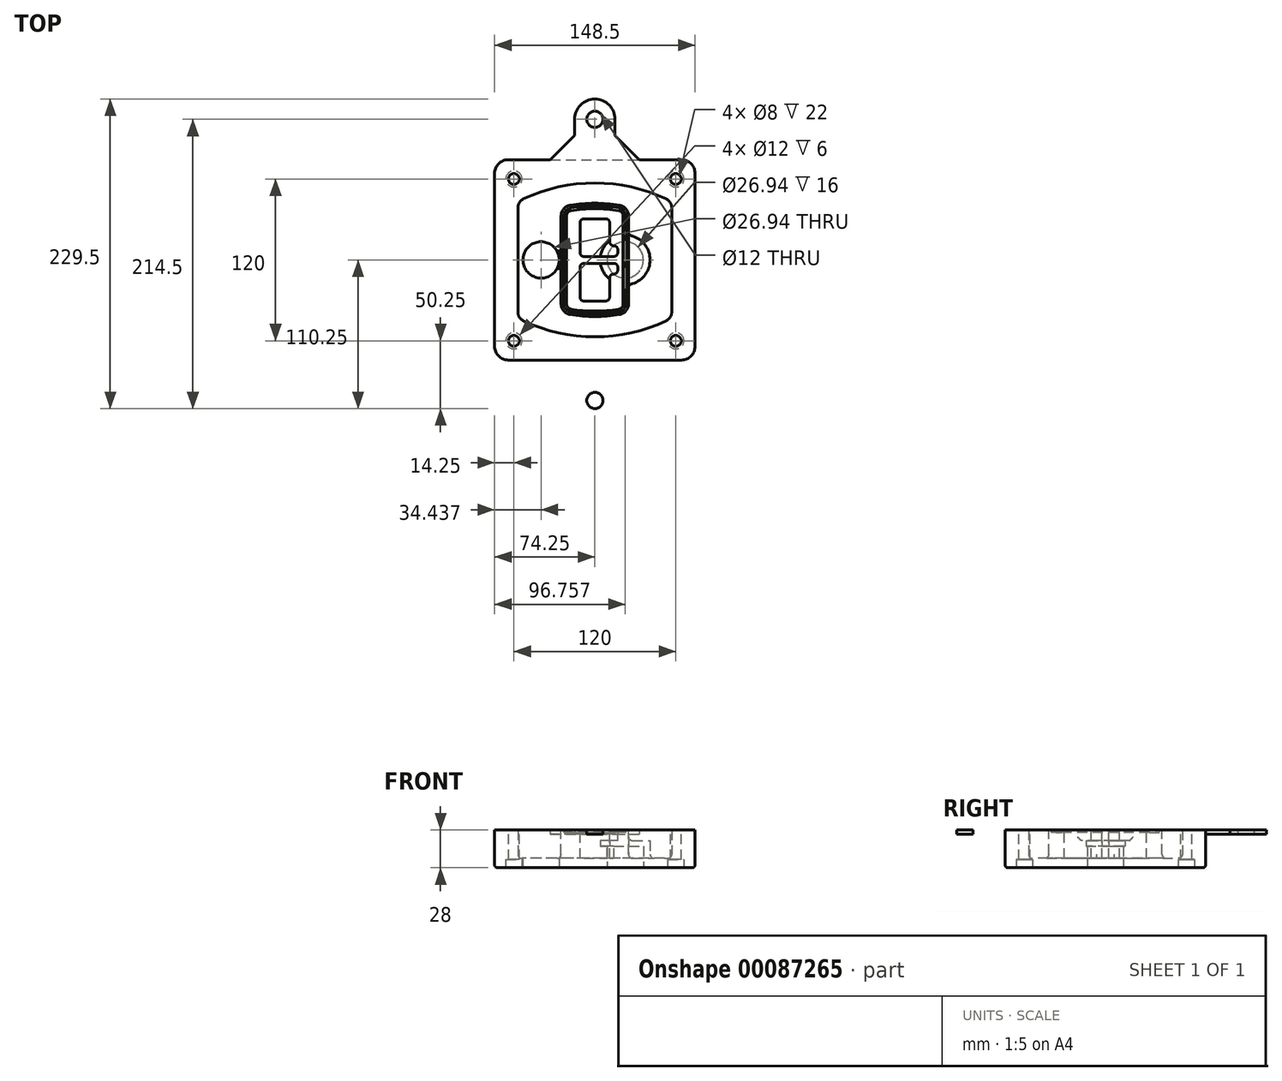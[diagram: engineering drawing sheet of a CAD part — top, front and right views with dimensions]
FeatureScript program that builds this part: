
annotation { "Feature Type Name" : "Feature", "Feature Type Description" : "" }
export const myFeature = defineFeature(function(context is Context, id is Id, definition is map)
    precondition{}
    {
        {
            var Q0;
            Q0=qCreatedBy(makeId("Top.planeOp"),FACE);
            var sketch = newSketch(context, id + "F0", { "sketchPlane" : qUnion([Q0])});
            skPoint(sketch, "E0.rect.middle", {"position": v(0, 0) * mm});
            skLineSegment(sketch, "E1.bottom", {"start": v(-64.25, -74.25) * mm, "end": v(64.25, -74.25) * mm});
            skLineSegment(sketch, "E1.top", {"start": v(-64.25, 74.25) * mm, "end": v(64.25, 74.25) * mm});
            skLineSegment(sketch, "E1.left", {"start": v(-74.25, -64.25) * mm, "end": v(-74.25, 64.25) * mm});
            skLineSegment(sketch, "E1.right", {"start": v(74.25, -64.25) * mm, "end": v(74.25, 64.25) * mm});
            skLineSegment(sketch, "E2", {"start": v(-74.25, 74.25) * mm, "end": v(74.25, -74.25) * mm, "construction": true});
            skLineSegment(sketch, "E3", {"start": v(74.25, 74.25) * mm, "end": v(-74.25, -74.25) * mm, "construction": true});
            skCircle(sketch, "E4", {"center": v(-60, 60) * mm, "radius": 4 * mm});
            skCircle(sketch, "E5", {"center": v(60, 60) * mm, "radius": 4 * mm});
            skCircle(sketch, "E6", {"center": v(60, -60) * mm, "radius": 4 * mm});
            skCircle(sketch, "E7", {"center": v(-60, -60) * mm, "radius": 4 * mm});
            skLineSegment(sketch, "E8", {"start": v(-60, 60) * mm, "end": v(60, 60) * mm, "construction": true});
            skLineSegment(sketch, "E9", {"start": v(60, 60) * mm, "end": v(60, -60) * mm, "construction": true});
            skLineSegment(sketch, "E10", {"start": v(60, -60) * mm, "end": v(-60, -60) * mm, "construction": true});
            skLineSegment(sketch, "E11", {"start": v(-60, -60) * mm, "end": v(-60, 60) * mm, "construction": true});
            skLineSegment(sketch, "E12", {"start": v(-60, 38.83) * mm, "end": v(-60, -38.83) * mm});
            skLineSegment(sketch, "E13", {"start": v(60, 38.83) * mm, "end": v(60, -38.83) * mm});
            skArc(sketch, "E14", {"start": v(54.26, 47.88) * mm, "mid": v(0, 60) * mm, "end": v(-54.26, 47.88) * mm});
            skArc(sketch, "E15", {"start": v(-54.26, -47.88) * mm, "mid": v(0, -60) * mm, "end": v(54.26, -47.88) * mm});
            skLineSegment(sketch, "E16", {"start": v(-60, 0) * mm, "end": v(60, 0) * mm, "construction": true});
            skPoint(sketch, "E17.visualSharp", {"position": v(-60, -45) * mm});
            skArc(sketch, "E17.filletArc", {"start": v(-60, -38.83) * mm, "mid": v(-58.44, -44.2) * mm, "end": v(-54.26, -47.88) * mm});
            skPoint(sketch, "E18.visualSharp", {"position": v(-60, 45) * mm});
            skArc(sketch, "E18.filletArc", {"start": v(-54.26, 47.88) * mm, "mid": v(-58.44, 44.2) * mm, "end": v(-60, 38.83) * mm});
            skPoint(sketch, "E19.visualSharp", {"position": v(60, 45) * mm});
            skArc(sketch, "E19.filletArc", {"start": v(60, 38.83) * mm, "mid": v(58.44, 44.2) * mm, "end": v(54.26, 47.88) * mm});
            skPoint(sketch, "E20.visualSharp", {"position": v(60, -45) * mm});
            skArc(sketch, "E20.filletArc", {"start": v(54.26, -47.88) * mm, "mid": v(58.44, -44.2) * mm, "end": v(60, -38.83) * mm});
            skPoint(sketch, "E21.visualSharp", {"position": v(-74.25, 74.25) * mm});
            skArc(sketch, "E21.filletArc", {"start": v(-64.25, 74.25) * mm, "mid": v(-71.32, 71.32) * mm, "end": v(-74.25, 64.25) * mm});
            skPoint(sketch, "E22.visualSharp", {"position": v(74.25, 74.25) * mm});
            skArc(sketch, "E22.filletArc", {"start": v(74.25, 64.25) * mm, "mid": v(71.32, 71.32) * mm, "end": v(64.25, 74.25) * mm});
            skPoint(sketch, "E23.visualSharp", {"position": v(74.25, -74.25) * mm});
            skArc(sketch, "E23.filletArc", {"start": v(64.25, -74.25) * mm, "mid": v(71.32, -71.32) * mm, "end": v(74.25, -64.25) * mm});
            skPoint(sketch, "E24.visualSharp", {"position": v(-74.25, -74.25) * mm});
            skArc(sketch, "E24.filletArc", {"start": v(-74.25, -64.25) * mm, "mid": v(-71.32, -71.32) * mm, "end": v(-64.25, -74.25) * mm});
            skArc(sketch, "E25.0", {"start": v(57, 38.83) * mm, "mid": v(55.9, 42.58) * mm, "end": v(52.98, 45.17) * mm});
            skLineSegment(sketch, "E25.1", {"start": v(57, 38.83) * mm, "end": v(57, -38.83) * mm});
            skArc(sketch, "E25.2", {"start": v(52.98, -45.17) * mm, "mid": v(55.9, -42.58) * mm, "end": v(57, -38.83) * mm});
            skArc(sketch, "E25.3", {"start": v(-52.98, -45.17) * mm, "mid": v(0, -57) * mm, "end": v(52.98, -45.17) * mm});
            skArc(sketch, "E25.4", {"start": v(-57, -38.83) * mm, "mid": v(-55.9, -42.58) * mm, "end": v(-52.98, -45.17) * mm});
            skArc(sketch, "E25.5", {"start": v(52.98, 45.17) * mm, "mid": v(0, 57) * mm, "end": v(-52.98, 45.17) * mm});
            skLineSegment(sketch, "E25.6", {"start": v(-57, 38.83) * mm, "end": v(-57, -38.83) * mm});
            skArc(sketch, "E25.7", {"start": v(-52.98, 45.17) * mm, "mid": v(-55.9, 42.58) * mm, "end": v(-57, 38.83) * mm});
            skArc(sketch, "E26.0", {"start": v(-55.96, 51.5) * mm, "mid": v(-61.82, 46.33) * mm, "end": v(-64, 38.83) * mm});
            skArc(sketch, "E26.1", {"start": v(55.96, 51.5) * mm, "mid": v(0, 64) * mm, "end": v(-55.96, 51.5) * mm});
            skArc(sketch, "E26.2", {"start": v(64, 38.83) * mm, "mid": v(61.82, 46.33) * mm, "end": v(55.96, 51.5) * mm});
            skLineSegment(sketch, "E26.3", {"start": v(64, 38.83) * mm, "end": v(64, -38.83) * mm});
            skArc(sketch, "E26.4", {"start": v(55.96, -51.5) * mm, "mid": v(61.82, -46.33) * mm, "end": v(64, -38.83) * mm});
            skLineSegment(sketch, "E26.5", {"start": v(-64, 38.83) * mm, "end": v(-64, -38.83) * mm});
            skArc(sketch, "E26.6", {"start": v(-55.96, -51.5) * mm, "mid": v(0, -64) * mm, "end": v(55.96, -51.5) * mm});
            skArc(sketch, "E26.7", {"start": v(-64, -38.83) * mm, "mid": v(-61.82, -46.33) * mm, "end": v(-55.96, -51.5) * mm});
            skSolve(sketch);
        }
        {
            var Q0;
            Q0=makeQuery(id+"F0.imprint","IMPRINT",FACE,{"disambiguationData":[TD([[makeQuery(id+"F0.imprint","IMPRINT",EDGE,{"derivedFrom":sQuery(id+"F0.wireOp",EDGE,"E1.bottom")}),1.0]])]});
            var Q1;
            Q1=makeQuery(id+"F0.imprint","IMPRINT",FACE,{"disambiguationData":[TD([[makeQuery(id+"F0.imprint","IMPRINT",EDGE,{"derivedFrom":sQuery(id+"F0.wireOp",EDGE,"E12")}),1.0]])]});
            var Q2;
            Q2=makeQuery(id+"F0.imprint","IMPRINT",FACE,{"disambiguationData":[TD([[makeQuery(id+"F0.imprint","IMPRINT",EDGE,{"derivedFrom":sQuery(id+"F0.wireOp",EDGE,"E25.0")}),1.0]])]});
            var Q3;
            Q3=makeQuery(id+"F0.imprint","IMPRINT",FACE,{"disambiguationData":[TD([[makeQuery(id+"F0.imprint","IMPRINT",EDGE,{"derivedFrom":sQuery(id+"F0.wireOp",EDGE,"E12")}),-1.0]])]});
            extrude(context, id + "F1", {"entities" : qUnion([Q0, Q1, Q2, Q3]), "oppositeDirection" : true, "depth" : 25 * mm});
        }
        {
            var Q0;
            Q0=makeQuery(id+"F0.imprint","IMPRINT",FACE,{"disambiguationData":[TD([[makeQuery(id+"F0.imprint","IMPRINT",EDGE,{"derivedFrom":sQuery(id+"F0.wireOp",EDGE,"E12")}),1.0]])]});
            extrude(context, id + "F2", {"entities" : qUnion([Q0]), "operationType" : NewBodyOperationType.ADD, "depth" : 3 * mm});
        }
        {
            var Q0;
            Q0=makeQuery(id+"F0.imprint","IMPRINT",FACE,{"disambiguationData":[TD([[makeQuery(id+"F0.imprint","IMPRINT",EDGE,{"derivedFrom":sQuery(id+"F0.wireOp",EDGE,"E25.0")}),1.0]])]});
            extrude(context, id + "F3", {"entities" : qUnion([Q0]), "operationType" : NewBodyOperationType.REMOVE, "oppositeDirection" : true, "depth" : 18 * mm});
        }
        {
            var Q0;
            Q0=makeQuery(id+"F2.opExtrude","CAP_FACE",FACE,{"disambiguationData":[OSD([sQuery(id+"F0.wireOp",EDGE,"E12"),sQuery(id+"F0.wireOp",EDGE,"E13"),sQuery(id+"F0.wireOp",EDGE,"E14"),sQuery(id+"F0.wireOp",EDGE,"E15"),sQuery(id+"F0.wireOp",EDGE,"E17.filletArc"),sQuery(id+"F0.wireOp",EDGE,"E18.filletArc"),sQuery(id+"F0.wireOp",EDGE,"E19.filletArc"),sQuery(id+"F0.wireOp",EDGE,"E20.filletArc"),sQuery(id+"F0.wireOp",EDGE,"E25.0"),sQuery(id+"F0.wireOp",EDGE,"E25.1"),sQuery(id+"F0.wireOp",EDGE,"E25.2"),sQuery(id+"F0.wireOp",EDGE,"E25.3"),sQuery(id+"F0.wireOp",EDGE,"E25.4"),sQuery(id+"F0.wireOp",EDGE,"E25.5"),sQuery(id+"F0.wireOp",EDGE,"E25.6"),sQuery(id+"F0.wireOp",EDGE,"E25.7")])],"isStart":false});
            var sketch = newSketch(context, id + "F4", { "sketchPlane" : qUnion([Q0])});
            skArc(sketch, "E27.0", {"start": v(-18.34, -40.45) * mm, "mid": v(0, -42) * mm, "end": v(18.34, -40.45) * mm});
            skArc(sketch, "E28.0", {"start": v(18.34, 40.45) * mm, "mid": v(0, 42) * mm, "end": v(-18.34, 40.45) * mm});
            skLineSegment(sketch, "E29", {"start": v(-25, 32.57) * mm, "end": v(-25, -32.57) * mm});
            skLineSegment(sketch, "E30", {"start": v(25, 32.57) * mm, "end": v(25, -32.57) * mm});
            skLineSegment(sketch, "E31", {"start": v(-25, 39.1) * mm, "end": v(25, 39.1) * mm, "construction": true});
            skLineSegment(sketch, "E32", {"start": v(-25, -39.1) * mm, "end": v(25, -39.1) * mm, "construction": true});
            skPoint(sketch, "E33.visualSharp", {"position": v(-25, 39.1) * mm});
            skArc(sketch, "E33.filletArc", {"start": v(-18.34, 40.45) * mm, "mid": v(-23.11, 37.73) * mm, "end": v(-25, 32.57) * mm});
            skPoint(sketch, "E34.visualSharp", {"position": v(25, 39.1) * mm});
            skArc(sketch, "E34.filletArc", {"start": v(25, 32.57) * mm, "mid": v(23.11, 37.73) * mm, "end": v(18.34, 40.45) * mm});
            skPoint(sketch, "E35.visualSharp", {"position": v(25, -39.1) * mm});
            skArc(sketch, "E35.filletArc", {"start": v(18.34, -40.45) * mm, "mid": v(23.11, -37.73) * mm, "end": v(25, -32.57) * mm});
            skPoint(sketch, "E36.visualSharp", {"position": v(-25, -39.1) * mm});
            skArc(sketch, "E36.filletArc", {"start": v(-25, -32.57) * mm, "mid": v(-23.11, -37.73) * mm, "end": v(-18.34, -40.45) * mm});
            skArc(sketch, "E37.0", {"start": v(52.98, 45.17) * mm, "mid": v(0, 57) * mm, "end": v(-52.98, 45.17) * mm});
            skArc(sketch, "E37.1", {"start": v(-52.98, 45.17) * mm, "mid": v(-55.9, 42.58) * mm, "end": v(-57, 38.83) * mm});
            skLineSegment(sketch, "E37.2", {"start": v(-57, 38.83) * mm, "end": v(-57, -38.83) * mm});
            skArc(sketch, "E37.3", {"start": v(-57, -38.83) * mm, "mid": v(-55.9, -42.58) * mm, "end": v(-52.98, -45.17) * mm});
            skArc(sketch, "E37.4", {"start": v(-52.98, -45.17) * mm, "mid": v(0, -57) * mm, "end": v(52.98, -45.17) * mm});
            skArc(sketch, "E37.5", {"start": v(52.98, -45.17) * mm, "mid": v(55.9, -42.58) * mm, "end": v(57, -38.83) * mm});
            skLineSegment(sketch, "E37.6", {"start": v(57, 38.83) * mm, "end": v(57, -38.83) * mm});
            skArc(sketch, "E37.7", {"start": v(57, 38.83) * mm, "mid": v(55.9, 42.58) * mm, "end": v(52.98, 45.17) * mm});
            skLineSegment(sketch, "E38.0", {"start": v(23, 32.57) * mm, "end": v(23, -32.57) * mm});
            skArc(sketch, "E38.1", {"start": v(18, -38.48) * mm, "mid": v(21.58, -36.44) * mm, "end": v(23, -32.57) * mm});
            skArc(sketch, "E38.2", {"start": v(-18, -38.48) * mm, "mid": v(0, -40) * mm, "end": v(18, -38.48) * mm});
            skArc(sketch, "E38.3", {"start": v(-23, -32.57) * mm, "mid": v(-21.58, -36.44) * mm, "end": v(-18, -38.48) * mm});
            skLineSegment(sketch, "E38.4", {"start": v(-23, 32.57) * mm, "end": v(-23, -32.57) * mm});
            skArc(sketch, "E38.5", {"start": v(23, 32.57) * mm, "mid": v(21.58, 36.44) * mm, "end": v(18, 38.48) * mm});
            skArc(sketch, "E38.6", {"start": v(-18, 38.48) * mm, "mid": v(-21.58, 36.44) * mm, "end": v(-23, 32.57) * mm});
            skArc(sketch, "E38.7", {"start": v(18, 38.48) * mm, "mid": v(0, 40) * mm, "end": v(-18, 38.48) * mm});
            skArc(sketch, "E39.0", {"start": v(21, 32.57) * mm, "mid": v(20.06, 35.15) * mm, "end": v(17.67, 36.5) * mm});
            skLineSegment(sketch, "E39.1", {"start": v(21, 32.57) * mm, "end": v(21, -32.57) * mm});
            skArc(sketch, "E39.2", {"start": v(17.67, -36.5) * mm, "mid": v(20.06, -35.15) * mm, "end": v(21, -32.57) * mm});
            skArc(sketch, "E39.3", {"start": v(-17.67, -36.5) * mm, "mid": v(0, -38) * mm, "end": v(17.67, -36.5) * mm});
            skArc(sketch, "E39.4", {"start": v(-21, -32.57) * mm, "mid": v(-20.06, -35.15) * mm, "end": v(-17.67, -36.5) * mm});
            skArc(sketch, "E39.5", {"start": v(17.67, 36.5) * mm, "mid": v(0, 38) * mm, "end": v(-17.67, 36.5) * mm});
            skLineSegment(sketch, "E39.6", {"start": v(-21, 32.57) * mm, "end": v(-21, -32.57) * mm});
            skArc(sketch, "E39.7", {"start": v(-17.67, 36.5) * mm, "mid": v(-20.06, 35.15) * mm, "end": v(-21, 32.57) * mm});
            skLineSegment(sketch, "E40", {"start": v(-25, 0) * mm, "end": v(25, 0) * mm, "construction": true});
            skLineSegment(sketch, "E41", {"start": v(-11, 5.5) * mm, "end": v(-11, 27.5) * mm});
            skLineSegment(sketch, "E42", {"start": v(-8, 30.5) * mm, "end": v(8, 30.5) * mm});
            skLineSegment(sketch, "E43", {"start": v(11, 27.5) * mm, "end": v(11, 13.5) * mm});
            skLineSegment(sketch, "E44", {"start": v(14, 10.5) * mm, "end": v(14, 10.5) * mm});
            skLineSegment(sketch, "E45", {"start": v(17, 7.5) * mm, "end": v(17, 5.5) * mm});
            skLineSegment(sketch, "E46", {"start": v(14, 2.5) * mm, "end": v(-8, 2.5) * mm});
            skPoint(sketch, "E47.visualSharp", {"position": v(-11, 30.5) * mm});
            skArc(sketch, "E47.filletArc", {"start": v(-8, 30.5) * mm, "mid": v(-10.12, 29.62) * mm, "end": v(-11, 27.5) * mm});
            skPoint(sketch, "E48.visualSharp", {"position": v(11, 30.5) * mm});
            skArc(sketch, "E48.filletArc", {"start": v(11, 27.5) * mm, "mid": v(10.12, 29.62) * mm, "end": v(8, 30.5) * mm});
            skPoint(sketch, "E49.visualSharp", {"position": v(11, 10.5) * mm});
            skArc(sketch, "E49.filletArc", {"start": v(11, 13.5) * mm, "mid": v(11.88, 11.38) * mm, "end": v(14, 10.5) * mm});
            skPoint(sketch, "E50.visualSharp", {"position": v(17, 10.5) * mm});
            skArc(sketch, "E50.filletArc", {"start": v(17, 7.5) * mm, "mid": v(16.12, 9.62) * mm, "end": v(14, 10.5) * mm});
            skPoint(sketch, "E51.visualSharp", {"position": v(17, 2.5) * mm});
            skArc(sketch, "E51.filletArc", {"start": v(14, 2.5) * mm, "mid": v(16.12, 3.38) * mm, "end": v(17, 5.5) * mm});
            skPoint(sketch, "E52.visualSharp", {"position": v(-11, 2.5) * mm});
            skArc(sketch, "E52.filletArc", {"start": v(-11, 5.5) * mm, "mid": v(-10.12, 3.38) * mm, "end": v(-8, 2.5) * mm});
            skLineSegment(sketch, "E53.0.MirrorCS", {"start": v(14, -2.5) * mm, "end": v(-8, -2.5) * mm});
            skArc(sketch, "E54.0.MirrorCS", {"start": v(-11, -5.5) * mm, "mid": v(-10.12, -3.38) * mm, "end": v(-8, -2.5) * mm});
            skLineSegment(sketch, "E55.0.MirrorCS", {"start": v(-11, -5.5) * mm, "end": v(-11, -27.5) * mm});
            skArc(sketch, "E56.0.MirrorCS", {"start": v(-8, -30.5) * mm, "mid": v(-10.12, -29.62) * mm, "end": v(-11, -27.5) * mm});
            skLineSegment(sketch, "E57.0.MirrorCS", {"start": v(-8, -30.5) * mm, "end": v(8, -30.5) * mm});
            skArc(sketch, "E58.0.MirrorCS", {"start": v(11, -27.5) * mm, "mid": v(10.12, -29.62) * mm, "end": v(8, -30.5) * mm});
            skLineSegment(sketch, "E59.0.MirrorCS", {"start": v(11, -27.5) * mm, "end": v(11, -13.5) * mm});
            skArc(sketch, "E60.0.MirrorCS", {"start": v(11, -13.5) * mm, "mid": v(11.88, -11.38) * mm, "end": v(14, -10.5) * mm});
            skArc(sketch, "E61.0.MirrorCS", {"start": v(17, -7.5) * mm, "mid": v(16.12, -9.62) * mm, "end": v(14, -10.5) * mm});
            skLineSegment(sketch, "E62.0.MirrorCS", {"start": v(17, -7.5) * mm, "end": v(17, -5.5) * mm});
            skArc(sketch, "E63.0.MirrorCS", {"start": v(14, -2.5) * mm, "mid": v(16.12, -3.38) * mm, "end": v(17, -5.5) * mm});
            skSolve(sketch);
        }
        {
            var Q0;
            Q0=makeQuery(id+"F4.imprint","IMPRINT",FACE,{"disambiguationData":[TD([[makeQuery(id+"F4.imprint","IMPRINT",EDGE,{"derivedFrom":sQuery(id+"F4.wireOp",EDGE,"E27.0")}),1.0]])]});
            var Q1;
            Q1=makeQuery(id+"F4.imprint","IMPRINT",FACE,{"disambiguationData":[TD([[makeQuery(id+"F4.imprint","IMPRINT",EDGE,{"derivedFrom":sQuery(id+"F4.wireOp",EDGE,"E38.0")}),-1.0]])]});
            var Q2;
            Q2=makeQuery(id+"F4.imprint","IMPRINT",FACE,{"disambiguationData":[TD([[makeQuery(id+"F4.imprint","IMPRINT",EDGE,{"derivedFrom":sQuery(id+"F4.wireOp",EDGE,"E39.0")}),1.0]])]});
            extrude(context, id + "F5", {"entities" : qUnion([Q0, Q1, Q2]), "operationType" : NewBodyOperationType.ADD, "endBound" : BoundingType.UP_TO_NEXT, "oppositeDirection" : true, "depth" : 25 * mm});
        }
        {
            var Q0;
            Q0=makeQuery(id+"F4.imprint","IMPRINT",FACE,{"disambiguationData":[TD([[makeQuery(id+"F4.imprint","IMPRINT",EDGE,{"derivedFrom":sQuery(id+"F4.wireOp",EDGE,"E38.0")}),-1.0]])]});
            extrude(context, id + "F6", {"entities" : qUnion([Q0]), "operationType" : NewBodyOperationType.REMOVE, "oppositeDirection" : true, "depth" : 2 * mm});
        }
        {
            var Q0;
            Q0=makeQuery(id+"F1.opExtrude","CAP_FACE",FACE,{"disambiguationData":[OSD([sQuery(id+"F0.wireOp",EDGE,"E1.bottom"),sQuery(id+"F0.wireOp",EDGE,"E1.top"),sQuery(id+"F0.wireOp",EDGE,"E1.left"),sQuery(id+"F0.wireOp",EDGE,"E1.right"),sQuery(id+"F0.wireOp",EDGE,"E4"),sQuery(id+"F0.wireOp",EDGE,"E5"),sQuery(id+"F0.wireOp",EDGE,"E6"),sQuery(id+"F0.wireOp",EDGE,"E7"),sQuery(id+"F0.wireOp",EDGE,"E21.filletArc"),sQuery(id+"F0.wireOp",EDGE,"E22.filletArc"),sQuery(id+"F0.wireOp",EDGE,"E23.filletArc"),sQuery(id+"F0.wireOp",EDGE,"E24.filletArc")])],"isStart":false});
            var sketch = newSketch(context, id + "F7", { "sketchPlane" : qUnion([Q0])});
            skCircle(sketch, "E64", {"center": v(22.5, 0) * mm, "radius": 13.47 * mm});
            skCircle(sketch, "E65", {"center": v(-39.81, 0) * mm, "radius": 13.47 * mm});
            skLineSegment(sketch, "E66", {"start": v(74.25, 0) * mm, "end": v(-74.25, 0) * mm});
            skCircle(sketch, "E67", {"center": v(22.5, 0) * mm, "radius": 18.47 * mm});
            skCircle(sketch, "E68", {"center": v(60, -60) * mm, "radius": 6 * mm});
            skCircle(sketch, "E69", {"center": v(-60, -60) * mm, "radius": 6 * mm});
            skCircle(sketch, "E70", {"center": v(-60, 60) * mm, "radius": 6 * mm});
            skCircle(sketch, "E71", {"center": v(60, 60) * mm, "radius": 6 * mm});
            skSolve(sketch);
        }
        {
            var Q0;
            {var subQ1=sQuery(id+"F7.wireOp",EDGE,"E66");var subQ4=sQuery(id+"F7.wireOp",EDGE,"E64");var subQ6=makeQuery(id+"F7.imprint","INTERSECT",VERTEX,{"disambiguationData":[OD(0.0)],"derivedFrom":[subQ4,subQ1]});Q0=makeQuery(id+"F7.imprint","IMPRINT",FACE,{"disambiguationData":[TD([[makeQuery(id+"F7.imprint","IMPRINT",EDGE,{"disambiguationData":[TD([[subQ6,-1.0]])],"derivedFrom":subQ4}),-1.0]])]});}
            var Q1;
            {var subQ0=sQuery(id+"F7.wireOp",EDGE,"E66");var subQ1=sQuery(id+"F7.wireOp",EDGE,"E64");var subQ3=makeQuery(id+"F7.imprint","INTERSECT",VERTEX,{"disambiguationData":[OD(0.0)],"derivedFrom":[subQ1,subQ0]});Q1=makeQuery(id+"F7.imprint","IMPRINT",FACE,{"disambiguationData":[TD([[makeQuery(id+"F7.imprint","IMPRINT",EDGE,{"disambiguationData":[TD([[subQ3,-1.0]])],"derivedFrom":subQ1}),1.0]])]});}
            var Q2;
            {var subQ0=sQuery(id+"F7.wireOp",EDGE,"E66");var subQ1=sQuery(id+"F7.wireOp",EDGE,"E64");var subQ3=makeQuery(id+"F7.imprint","INTERSECT",VERTEX,{"disambiguationData":[OD(0.0)],"derivedFrom":[subQ1,subQ0]});Q2=makeQuery(id+"F7.imprint","IMPRINT",FACE,{"disambiguationData":[TD([[makeQuery(id+"F7.imprint","IMPRINT",EDGE,{"disambiguationData":[TD([[subQ3,1.0]])],"derivedFrom":subQ1}),1.0]])]});}
            var Q3;
            {var subQ1=sQuery(id+"F7.wireOp",EDGE,"E66");var subQ4=sQuery(id+"F7.wireOp",EDGE,"E64");var subQ6=makeQuery(id+"F7.imprint","INTERSECT",VERTEX,{"disambiguationData":[OD(0.0)],"derivedFrom":[subQ4,subQ1]});Q3=makeQuery(id+"F7.imprint","IMPRINT",FACE,{"disambiguationData":[TD([[makeQuery(id+"F7.imprint","IMPRINT",EDGE,{"disambiguationData":[TD([[subQ6,1.0]])],"derivedFrom":subQ4}),-1.0]])]});}
            extrude(context, id + "F8", {"entities" : qUnion([Q0, Q1, Q2, Q3]), "operationType" : NewBodyOperationType.ADD, "oppositeDirection" : true, "depth" : 20 * mm});
        }
        {
            var Q0;
            {var subQ0=sQuery(id+"F7.wireOp",EDGE,"E66");var subQ1=sQuery(id+"F7.wireOp",EDGE,"E64");var subQ3=makeQuery(id+"F7.imprint","INTERSECT",VERTEX,{"disambiguationData":[OD(0.0)],"derivedFrom":[subQ1,subQ0]});Q0=makeQuery(id+"F7.imprint","IMPRINT",FACE,{"disambiguationData":[TD([[makeQuery(id+"F7.imprint","IMPRINT",EDGE,{"disambiguationData":[TD([[subQ3,-1.0]])],"derivedFrom":subQ1}),1.0]])]});}
            var Q1;
            {var subQ0=sQuery(id+"F7.wireOp",EDGE,"E66");var subQ1=sQuery(id+"F7.wireOp",EDGE,"E64");var subQ3=makeQuery(id+"F7.imprint","INTERSECT",VERTEX,{"disambiguationData":[OD(0.0)],"derivedFrom":[subQ1,subQ0]});Q1=makeQuery(id+"F7.imprint","IMPRINT",FACE,{"disambiguationData":[TD([[makeQuery(id+"F7.imprint","IMPRINT",EDGE,{"disambiguationData":[TD([[subQ3,1.0]])],"derivedFrom":subQ1}),1.0]])]});}
            extrude(context, id + "F9", {"entities" : qUnion([Q0, Q1]), "operationType" : NewBodyOperationType.REMOVE, "oppositeDirection" : true, "depth" : 16 * mm});
        }
        {
            var Q0;
            {var subQ0=sQuery(id+"F7.wireOp",EDGE,"E66");var subQ1=sQuery(id+"F7.wireOp",EDGE,"E65");var subQ3=makeQuery(id+"F7.imprint","INTERSECT",VERTEX,{"disambiguationData":[OD(0.0)],"derivedFrom":[subQ1,subQ0]});Q0=makeQuery(id+"F7.imprint","IMPRINT",FACE,{"disambiguationData":[TD([[makeQuery(id+"F7.imprint","IMPRINT",EDGE,{"disambiguationData":[TD([[subQ3,-1.0]])],"derivedFrom":subQ1}),1.0]])]});}
            var Q1;
            {var subQ0=sQuery(id+"F7.wireOp",EDGE,"E66");var subQ1=sQuery(id+"F7.wireOp",EDGE,"E65");var subQ3=makeQuery(id+"F7.imprint","INTERSECT",VERTEX,{"disambiguationData":[OD(0.0)],"derivedFrom":[subQ1,subQ0]});Q1=makeQuery(id+"F7.imprint","IMPRINT",FACE,{"disambiguationData":[TD([[makeQuery(id+"F7.imprint","IMPRINT",EDGE,{"disambiguationData":[TD([[subQ3,1.0]])],"derivedFrom":subQ1}),1.0]])]});}
            extrude(context, id + "F10", {"entities" : qUnion([Q0, Q1]), "operationType" : NewBodyOperationType.REMOVE, "oppositeDirection" : true, "depth" : 25 * mm});
        }
        {
            var Q0;
            Q0=makeQuery(id+"F7.imprint","IMPRINT",FACE,{"disambiguationData":[TD([[makeQuery(id+"F7.imprint","IMPRINT",EDGE,{"derivedFrom":sQuery(id+"F7.wireOp",EDGE,"E68")}),1.0]])]});
            var Q1;
            Q1=makeQuery(id+"F7.imprint","IMPRINT",FACE,{"disambiguationData":[TD([[makeQuery(id+"F7.imprint","IMPRINT",EDGE,{"derivedFrom":makeQuery(id+"F1.opExtrude","CAP_EDGE",EDGE,{"disambiguationData":[OSD([sQuery(id+"F0.wireOp",EDGE,"E5")])],"isStart":false})}),-1.0]])]});
            var Q2;
            Q2=makeQuery(id+"F7.imprint","IMPRINT",FACE,{"disambiguationData":[TD([[makeQuery(id+"F7.imprint","IMPRINT",EDGE,{"derivedFrom":sQuery(id+"F7.wireOp",EDGE,"E69")}),1.0]])]});
            var Q3;
            Q3=makeQuery(id+"F7.imprint","IMPRINT",FACE,{"disambiguationData":[TD([[makeQuery(id+"F7.imprint","IMPRINT",EDGE,{"derivedFrom":makeQuery(id+"F1.opExtrude","CAP_EDGE",EDGE,{"disambiguationData":[OSD([sQuery(id+"F0.wireOp",EDGE,"E4")])],"isStart":false})}),-1.0]])]});
            var Q4;
            Q4=makeQuery(id+"F7.imprint","IMPRINT",FACE,{"disambiguationData":[TD([[makeQuery(id+"F7.imprint","IMPRINT",EDGE,{"derivedFrom":sQuery(id+"F7.wireOp",EDGE,"E70")}),1.0]])]});
            var Q5;
            Q5=makeQuery(id+"F7.imprint","IMPRINT",FACE,{"disambiguationData":[TD([[makeQuery(id+"F7.imprint","IMPRINT",EDGE,{"derivedFrom":makeQuery(id+"F1.opExtrude","CAP_EDGE",EDGE,{"disambiguationData":[OSD([sQuery(id+"F0.wireOp",EDGE,"E7")])],"isStart":false})}),-1.0]])]});
            var Q6;
            Q6=makeQuery(id+"F7.imprint","IMPRINT",FACE,{"disambiguationData":[TD([[makeQuery(id+"F7.imprint","IMPRINT",EDGE,{"derivedFrom":sQuery(id+"F7.wireOp",EDGE,"E71")}),1.0]])]});
            var Q7;
            Q7=makeQuery(id+"F7.imprint","IMPRINT",FACE,{"disambiguationData":[TD([[makeQuery(id+"F7.imprint","IMPRINT",EDGE,{"derivedFrom":makeQuery(id+"F1.opExtrude","CAP_EDGE",EDGE,{"disambiguationData":[OSD([sQuery(id+"F0.wireOp",EDGE,"E6")])],"isStart":false})}),-1.0]])]});
            extrude(context, id + "F11", {"entities" : qUnion([Q0, Q1, Q2, Q3, Q4, Q5, Q6, Q7]), "operationType" : NewBodyOperationType.REMOVE, "oppositeDirection" : true, "depth" : 6 * mm});
        }
        {
            var Q0;
            Q0=makeQuery(id+"F9.boolean.opBoolean","COPY",FACE,{"derivedFrom":makeQuery(id+"F9.opExtrude","CAP_FACE",FACE,{"disambiguationData":[OSD([sQuery(id+"F7.wireOp",EDGE,"E64")])],"isStart":false})});
            var sketch = newSketch(context, id + "F12", { "sketchPlane" : qUnion([Q0])});
            skArc(sketch, "E72.0", {"start": v(11, 14.45) * mm, "mid": v(6.45, 9.13) * mm, "end": v(4.2, 2.5) * mm});
            skArc(sketch, "E72.1", {"start": v(4.2, -2.5) * mm, "mid": v(6.45, -9.13) * mm, "end": v(11, -14.45) * mm});
            skLineSegment(sketch, "E73", {"start": v(4.2, -2.5) * mm, "end": v(14, -2.5) * mm});
            skLineSegment(sketch, "E74.0", {"start": v(14, 2.5) * mm, "end": v(4.2, 2.5) * mm});
            skArc(sketch, "E74.1", {"start": v(14, 2.5) * mm, "mid": v(16.12, 3.38) * mm, "end": v(17, 5.5) * mm});
            skLineSegment(sketch, "E74.2", {"start": v(17, 7.5) * mm, "end": v(17, 5.5) * mm});
            skArc(sketch, "E74.3", {"start": v(17, 7.5) * mm, "mid": v(16.12, 9.62) * mm, "end": v(14, 10.5) * mm});
            skArc(sketch, "E74.4", {"start": v(11, 13.5) * mm, "mid": v(11.88, 11.38) * mm, "end": v(14, 10.5) * mm});
            skLineSegment(sketch, "E74.5", {"start": v(11, 14.45) * mm, "end": v(11, 13.5) * mm});
            skLineSegment(sketch, "E74.7", {"start": v(14, -2.5) * mm, "end": v(4.2, -2.5) * mm});
            skArc(sketch, "E74.8", {"start": v(14, -2.5) * mm, "mid": v(16.12, -3.38) * mm, "end": v(17, -5.5) * mm});
            skLineSegment(sketch, "E74.9", {"start": v(17, -7.5) * mm, "end": v(17, -5.5) * mm});
            skArc(sketch, "E74.10", {"start": v(17, -7.5) * mm, "mid": v(16.12, -9.62) * mm, "end": v(14, -10.5) * mm});
            skArc(sketch, "E74.11", {"start": v(11, -13.5) * mm, "mid": v(11.88, -11.38) * mm, "end": v(14, -10.5) * mm});
            skLineSegment(sketch, "E74.12", {"start": v(11, -14.45) * mm, "end": v(11, -13.5) * mm});
            skPoint(sketch, "E75.orphan", {"position": v(11, -27.5) * mm});
            skPoint(sketch, "E76.orphan", {"position": v(-8, -2.5) * mm});
            skPoint(sketch, "E77.orphan", {"position": v(-8, 2.5) * mm});
            skPoint(sketch, "E78.orphan", {"position": v(11, 27.5) * mm});
            skSolve(sketch);
        }
        {
            var Q0;
            {var subQ7=sQuery(id+"F12.wireOp",EDGE,"E72.0");var subQ14=sQuery(id+"F12.wireOp",EDGE,"E72.1");var subQ16=sQuery(id+"F12.wireOp",EDGE,"E74.1");var subQ18=sQuery(id+"F12.wireOp",EDGE,"E74.8");Q0=qUnion([makeQuery(id+"F12.imprint","IMPRINT",FACE,{"disambiguationData":[TD([[makeQuery(id+"F12.imprint","IMPRINT",EDGE,{"derivedFrom":subQ7}),1.0]])]}),makeQuery(id+"F12.imprint","IMPRINT",FACE,{"disambiguationData":[TD([[makeQuery(id+"F12.imprint","IMPRINT",EDGE,{"derivedFrom":subQ14}),1.0]])]}),makeQuery(id+"F12.imprint","IMPRINT",FACE,{"disambiguationData":[TD([[makeQuery(id+"F12.imprint","IMPRINT",EDGE,{"derivedFrom":subQ16}),1.0]])]}),makeQuery(id+"F12.imprint","IMPRINT",FACE,{"disambiguationData":[TD([[makeQuery(id+"F12.imprint","IMPRINT",EDGE,{"derivedFrom":subQ18}),-1.0]])]})]);}
            var Q1;
            Q1=makeQuery(id+"F5.boolean.opBoolean","SPLIT",FACE,{"disambiguationData":[TD([makeQuery(id+"F5.opExtrude","SWEPT_FACE",FACE,{"disambiguationData":[OSD([sQuery(id+"F4.wireOp",EDGE,"E41")])]})])],"derivedFrom":makeQuery(id+"F3.boolean.opBoolean","COPY",FACE,{"derivedFrom":makeQuery(id+"F3.opExtrude","CAP_FACE",FACE,{"disambiguationData":[OSD([sQuery(id+"F0.wireOp",EDGE,"E25.0"),sQuery(id+"F0.wireOp",EDGE,"E25.1"),sQuery(id+"F0.wireOp",EDGE,"E25.2"),sQuery(id+"F0.wireOp",EDGE,"E25.3"),sQuery(id+"F0.wireOp",EDGE,"E25.4"),sQuery(id+"F0.wireOp",EDGE,"E25.5"),sQuery(id+"F0.wireOp",EDGE,"E25.6"),sQuery(id+"F0.wireOp",EDGE,"E25.7")])],"isStart":false})})});
            extrude(context, id + "F13", {"entities" : qUnion([Q0]), "operationType" : NewBodyOperationType.REMOVE, "endBound" : BoundingType.UP_TO_SURFACE, "endBoundEntityFace" : qUnion([Q1]), "depth" : 25 * mm});
        }
        {
            var Q0;
            Q0=makeQuery(id+"F3.boolean.opBoolean","COPY",EDGE,{"derivedFrom":makeQuery(id+"F3.opExtrude","CAP_EDGE",EDGE,{"disambiguationData":[OSD([sQuery(id+"F0.wireOp",EDGE,"E25.6")])],"isStart":false})});
            var Q1;
            Q1=makeQuery(id+"F8.boolean.opBoolean","INTERSECT",EDGE,{"derivedFrom":[makeQuery(id+"F5.opExtrude","SWEPT_FACE",FACE,{"disambiguationData":[OSD([sQuery(id+"F4.wireOp",EDGE,"E30")])]}),makeQuery(id+"F8.opExtrude","CAP_FACE",FACE,{"disambiguationData":[OSD([sQuery(id+"F7.wireOp",EDGE,"E67")])],"isStart":false})]});
            var Q2;
            Q2=makeQuery(id+"F8.boolean.opBoolean","INTERSECT",EDGE,{"disambiguationData":[OD(1.0)],"derivedFrom":[makeQuery(id+"F5.opExtrude","SWEPT_FACE",FACE,{"disambiguationData":[OSD([sQuery(id+"F4.wireOp",EDGE,"E30")])]}),makeQuery(id+"F8.opExtrude","SWEPT_FACE",FACE,{"disambiguationData":[OSD([sQuery(id+"F7.wireOp",EDGE,"E67")])]})]});
            var Q3;
            {var subQ0=sQuery(id+"F4.wireOp",EDGE,"E30");Q3=makeQuery(id+"F8.boolean.opBoolean","SPLIT",EDGE,{"disambiguationData":[TD([makeQuery(id+"F5.opExtrude","SWEPT_FACE",FACE,{"disambiguationData":[OSD([sQuery(id+"F4.wireOp",EDGE,"E35.filletArc")])]})])],"derivedFrom":makeQuery(id+"F5.opExtrude","CAP_EDGE",EDGE,{"disambiguationData":[OSD([subQ0])],"isStart":false})});}
            var Q4;
            {var subQ0=sQuery(id+"F0.wireOp",EDGE,"E25.7");var subQ1=sQuery(id+"F0.wireOp",EDGE,"E25.1");var subQ2=sQuery(id+"F0.wireOp",EDGE,"E25.6");var subQ3=sQuery(id+"F0.wireOp",EDGE,"E25.5");var subQ4=sQuery(id+"F0.wireOp",EDGE,"E25.4");var subQ5=sQuery(id+"F0.wireOp",EDGE,"E25.0");var subQ6=sQuery(id+"F0.wireOp",EDGE,"E25.2");var subQ7=sQuery(id+"F0.wireOp",EDGE,"E25.3");Q4=makeQuery(id+"F8.boolean.opBoolean","INTERSECT",EDGE,{"derivedFrom":[makeQuery(id+"F5.boolean.opBoolean","SPLIT",FACE,{"disambiguationData":[TD([makeQuery(id+"F2.opExtrude","SWEPT_FACE",FACE,{"disambiguationData":[OSD([subQ5])]})])],"derivedFrom":makeQuery(id+"F3.boolean.opBoolean","COPY",FACE,{"derivedFrom":makeQuery(id+"F3.opExtrude","CAP_FACE",FACE,{"disambiguationData":[OSD([subQ5,subQ1,subQ6,subQ7,subQ4,subQ3,subQ2,subQ0])],"isStart":false})})}),makeQuery(id+"F8.opExtrude","SWEPT_FACE",FACE,{"disambiguationData":[OSD([sQuery(id+"F7.wireOp",EDGE,"E67")])]})]});}
            var Q5;
            Q5=makeQuery(id+"F8.boolean.opBoolean","INTERSECT",EDGE,{"disambiguationData":[OD(0.0)],"derivedFrom":[makeQuery(id+"F5.opExtrude","SWEPT_FACE",FACE,{"disambiguationData":[OSD([sQuery(id+"F4.wireOp",EDGE,"E30")])]}),makeQuery(id+"F8.opExtrude","SWEPT_FACE",FACE,{"disambiguationData":[OSD([sQuery(id+"F7.wireOp",EDGE,"E67")])]})]});
            fillet(context, id + "F14", {"entities" : qUnion([Q0, Q1, Q2, Q3, Q4, Q5]), "radius" : 3 * mm, "tangentPropagation" : true, "allowEdgeOverflow" : false});
        }
        {
            var Q0;
            Q0=makeQuery(id+"F1.opExtrude","CAP_EDGE",EDGE,{"disambiguationData":[OSD([sQuery(id+"F0.wireOp",EDGE,"E1.bottom")])],"isStart":false});
            fillet(context, id + "F15", {"entities" : qUnion([Q0]), "radius" : 2 * mm, "tangentPropagation" : true, "allowEdgeOverflow" : false});
        }
        {
            var Q0;
            {var subQ0=sQuery(id+"F0.wireOp",EDGE,"E22.filletArc");var subQ1=sQuery(id+"F0.wireOp",EDGE,"E7");var subQ2=sQuery(id+"F0.wireOp",EDGE,"E6");var subQ3=sQuery(id+"F0.wireOp",EDGE,"E5");var subQ4=sQuery(id+"F0.wireOp",EDGE,"E4");var subQ5=sQuery(id+"F0.wireOp",EDGE,"E1.bottom");var subQ6=sQuery(id+"F0.wireOp",EDGE,"E21.filletArc");var subQ7=sQuery(id+"F0.wireOp",EDGE,"E1.top");var subQ8=sQuery(id+"F0.wireOp",EDGE,"E1.left");var subQ9=sQuery(id+"F0.wireOp",EDGE,"E1.right");var subQ10=sQuery(id+"F0.wireOp",EDGE,"E23.filletArc");var subQ11=sQuery(id+"F0.wireOp",EDGE,"E24.filletArc");Q0=makeQuery(id+"F2.boolean.opBoolean","SPLIT",FACE,{"disambiguationData":[TD([makeQuery(id+"F1.opExtrude","SWEPT_FACE",FACE,{"disambiguationData":[OSD([subQ5])]})])],"derivedFrom":makeQuery(id+"F1.opExtrude","CAP_FACE",FACE,{"disambiguationData":[OSD([subQ5,subQ7,subQ8,subQ9,subQ4,subQ3,subQ2,subQ1,subQ6,subQ0,subQ10,subQ11])],"isStart":true})});}
            var sketch = newSketch(context, id + "F16", { "sketchPlane" : qUnion([Q0])});
            skCircle(sketch, "E79", {"center": v(0, 104.25) * mm, "radius": 6 * mm});
            skArc(sketch, "E80", {"start": v(15, 104.25) * mm, "mid": v(0, 119.25) * mm, "end": v(-15, 104.25) * mm});
            skLineSegment(sketch, "E81", {"start": v(15, 104.25) * mm, "end": v(15, 92.25) * mm});
            skLineSegment(sketch, "E82", {"start": v(-15, 104.25) * mm, "end": v(-15, 92.25) * mm});
            skLineSegment(sketch, "E83", {"start": v(15, 92.25) * mm, "end": v(33, 74.25) * mm});
            skLineSegment(sketch, "E84", {"start": v(-15, 92.25) * mm, "end": v(-33, 74.25) * mm});
            skCircle(sketch, "E85.MirrorC", {"center": v(0, -104.25) * mm, "radius": 6 * mm});
            skLineSegment(sketch, "E86.MirrorCS", {"start": v(-15, -104.25) * mm, "end": v(-15, -92.25) * mm});
            skLineSegment(sketch, "E87.MirrorCS", {"start": v(15, -92.25) * mm, "end": v(33, -74.25) * mm});
            skLineSegment(sketch, "E88.MirrorCS", {"start": v(-15, -92.25) * mm, "end": v(-33, -74.25) * mm});
            skLineSegment(sketch, "E89.MirrorCS", {"start": v(15, -104.25) * mm, "end": v(15, -92.25) * mm});
            skArc(sketch, "E90.MirrorCS", {"start": v(15, -104.25) * mm, "mid": v(0, -119.25) * mm, "end": v(-15, -104.25) * mm});
            skSolve(sketch);
        }
        {
            var Q0;
            Q0=makeQuery(id+"F16.imprint","IMPRINT",FACE,{"disambiguationData":[TD([[makeQuery(id+"F16.imprint","IMPRINT",EDGE,{"derivedFrom":makeQuery(id+"F1.opExtrude","CAP_EDGE",EDGE,{"disambiguationData":[OSD([sQuery(id+"F0.wireOp",EDGE,"E1.left")])],"isStart":true})}),-1.0]])]});
            var Q1;
            Q1=makeQuery(id+"F16.imprint","IMPRINT",FACE,{"disambiguationData":[TD([[makeQuery(id+"F16.imprint","IMPRINT",EDGE,{"derivedFrom":sQuery(id+"F16.wireOp",EDGE,"E79")}),-1.0]])]});
            var Q2;
            Q2=makeQuery(id+"F16.imprint","IMPRINT",FACE,{"disambiguationData":[TD([[makeQuery(id+"F16.imprint","IMPRINT",EDGE,{"derivedFrom":sQuery(id+"F16.wireOp",EDGE,"E85.MirrorC")}),1.0]])]});
            var Q3;
            Q3=makeQuery(id+"F2.opExtrude","CAP_FACE",FACE,{"disambiguationData":[OSD([sQuery(id+"F0.wireOp",EDGE,"E12"),sQuery(id+"F0.wireOp",EDGE,"E13"),sQuery(id+"F0.wireOp",EDGE,"E14"),sQuery(id+"F0.wireOp",EDGE,"E15"),sQuery(id+"F0.wireOp",EDGE,"E17.filletArc"),sQuery(id+"F0.wireOp",EDGE,"E18.filletArc"),sQuery(id+"F0.wireOp",EDGE,"E19.filletArc"),sQuery(id+"F0.wireOp",EDGE,"E20.filletArc"),sQuery(id+"F0.wireOp",EDGE,"E25.0"),sQuery(id+"F0.wireOp",EDGE,"E25.1"),sQuery(id+"F0.wireOp",EDGE,"E25.2"),sQuery(id+"F0.wireOp",EDGE,"E25.3"),sQuery(id+"F0.wireOp",EDGE,"E25.4"),sQuery(id+"F0.wireOp",EDGE,"E25.5"),sQuery(id+"F0.wireOp",EDGE,"E25.6"),sQuery(id+"F0.wireOp",EDGE,"E25.7")])],"isStart":false});
            extrude(context, id + "F17", {"entities" : qUnion([Q0, Q1, Q2]), "operationType" : NewBodyOperationType.ADD, "endBound" : BoundingType.UP_TO_SURFACE, "endBoundEntityFace" : qUnion([Q3]), "depth" : 25 * mm});
        }
    });
